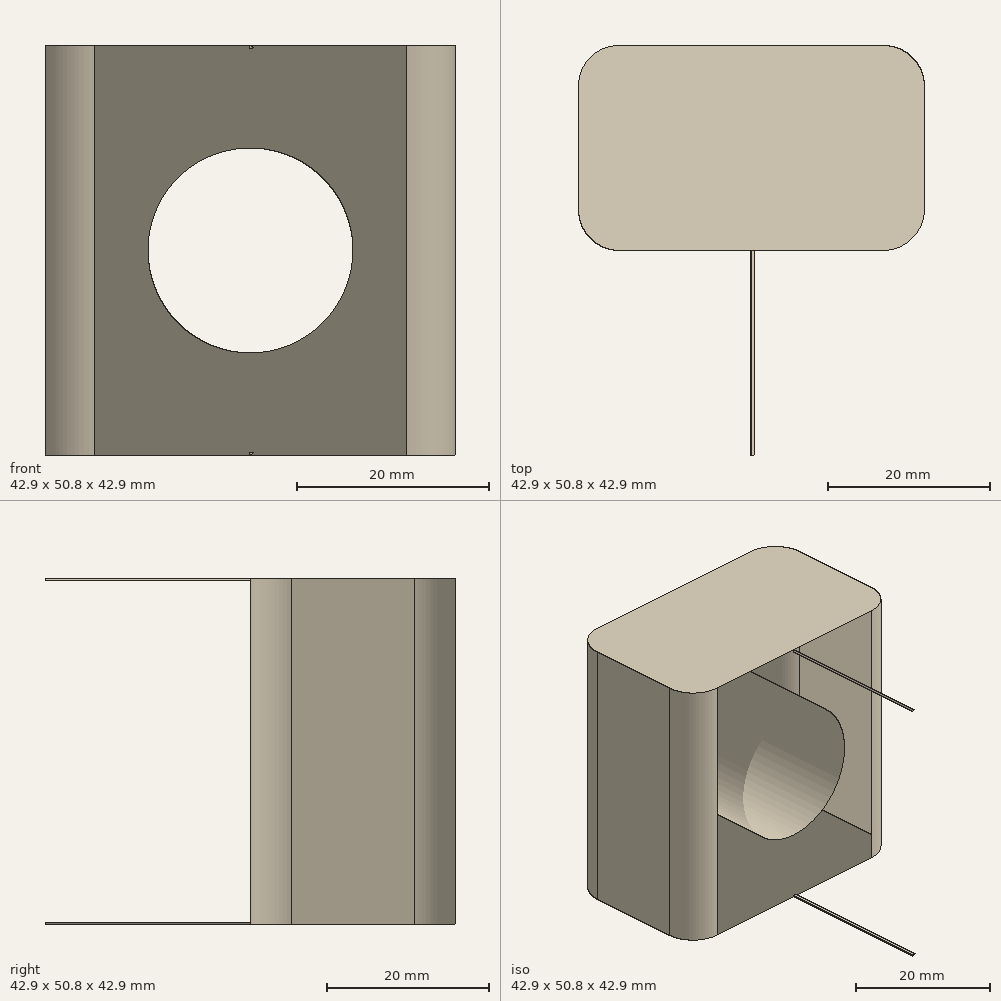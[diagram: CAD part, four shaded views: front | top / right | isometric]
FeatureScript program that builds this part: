
annotation { "Feature Type Name" : "Feature", "Feature Type Description" : "" }
export const myFeature = defineFeature(function(context is Context, id is Id, definition is map)
    precondition{}
    {
        {
            var Q0;
            Q0=qCreatedBy(makeId("Front.planeOp"),FACE);
            var sketch = newSketch(context, id + "F0", { "sketchPlane" : qUnion([Q0])});
            skLineSegment(sketch, "E0.bottom", {"start": v(-21.44, 21.44) * mm, "end": v(21.44, 21.44) * mm});
            skLineSegment(sketch, "E0.top", {"start": v(-21.44, -21.44) * mm, "end": v(21.44, -21.44) * mm});
            skLineSegment(sketch, "E0.left", {"start": v(-21.44, 21.44) * mm, "end": v(-21.44, -21.44) * mm});
            skLineSegment(sketch, "E0.right", {"start": v(21.44, 21.44) * mm, "end": v(21.44, -21.44) * mm});
            skPoint(sketch, "E0.middle", {"position": v(0, 0) * mm});
            skCircle(sketch, "E1", {"center": v(0, 0) * mm, "radius": 10.72 * mm});
            skSolve(sketch);
        }
        {
            var Q0;
            Q0=makeQuery(id+"F0.imprint","IMPRINT",FACE,{"disambiguationData":[TD([[makeQuery(id+"F0.imprint","IMPRINT",EDGE,{"derivedFrom":sQuery(id+"F0.wireOp",EDGE,"E0.bottom")}),-1.0]])]});
            extrude(context, id + "F1", {"entities" : qUnion([Q0]), "depth" : 25.4 * mm, "offsetDistance" : 25.4 * mm});
        }
        {
            var Q0;
            Q0=makeQuery(id+"F1.opExtrude","CAP_FACE",FACE,{"disambiguationData":[OSD([sQuery(id+"F0.wireOp",EDGE,"E0.bottom"),sQuery(id+"F0.wireOp",EDGE,"E0.top"),sQuery(id+"F0.wireOp",EDGE,"E0.left"),sQuery(id+"F0.wireOp",EDGE,"E0.right"),sQuery(id+"F0.wireOp",EDGE,"E1")])],"isStart":false});
            var sketch = newSketch(context, id + "F2", { "sketchPlane" : qUnion([Q0])});
            skFitSpline(sketch, "E2.MirrorC", {"points": [v(0, -21.44) * mm, v(-31.8, -40.34) * mm, v(-17.9, -101.47) * mm, v(-24.58, -66.76) * mm, v(-14.18, -69.87) * mm, v(-23.15, -57.45) * mm, v(21.44, -85.42) * mm, v(-17.46, -47.72) * mm, v(9.77, -59.73) * mm, v(-11.7, -36.11) * mm, v(0, -21.44) * mm]});
            skFitSpline(sketch, "E3.MirrorC", {"points": [v(0, -21.44) * mm, v(10.1, -51.1) * mm, v(56.97, -85.03) * mm, v(23.52, -53.99) * mm, v(53.05, -53.56) * mm, v(16.41, -38.66) * mm, v(46.61, -40.4) * mm, v(14.47, -25.9) * mm, v(0, -21.44) * mm]});
            skLineSegment(sketch, "E4.0", {"start": v(-21.44, -21.44) * mm, "end": v(-6.5, -21.44) * mm});
            skLineSegment(sketch, "E5.trimOffspring", {"start": v(4.65, -21.44) * mm, "end": v(21.44, -21.44) * mm});
            skLineSegment(sketch, "E6", {"start": v(-0.18, -21.15) * mm, "end": v(0.33, -21.15) * mm});
            skSolve(sketch);
        }
        {
            var Q0;
            Q0=makeQuery(id+"F1.opExtrude","CAP_EDGE",EDGE,{"disambiguationData":[OSD([sQuery(id+"F0.wireOp",EDGE,"E0.right")])],"isStart":true});
            var Q1;
            Q1=makeQuery(id+"F1.opExtrude","CAP_EDGE",EDGE,{"disambiguationData":[OSD([sQuery(id+"F0.wireOp",EDGE,"E0.right")])],"isStart":false});
            var Q2;
            Q2=makeQuery(id+"F1.opExtrude","CAP_EDGE",EDGE,{"disambiguationData":[OSD([sQuery(id+"F0.wireOp",EDGE,"E0.left")])],"isStart":true});
            var Q3;
            Q3=makeQuery(id+"F1.opExtrude","CAP_EDGE",EDGE,{"disambiguationData":[OSD([sQuery(id+"F0.wireOp",EDGE,"E0.left")])],"isStart":false});
            fillet(context, id + "F3", {"entities" : qUnion([Q0, Q1, Q2, Q3]), "radius" : 5.08 * mm, "tangentPropagation" : true, "allowEdgeOverflow" : false});
        }
        {
            var Q0;
            {var subQ4=sQuery(id+"F2.wireOp",EDGE,"E2.MirrorC");var subQ6=makeQuery(id+"F2.imprint","IMPRINT",VERTEX,{"derivedFrom":subQ4});Q0=makeQuery(id+"F2.imprint","IMPRINT",FACE,{"disambiguationData":[TD([[makeQuery(id+"F2.imprint","IMPRINT",EDGE,{"disambiguationData":[TD([[subQ6,-1.0]])],"derivedFrom":subQ4}),1.0]])]});}
            var Q1;
            {var subQ0=sQuery(id+"F2.wireOp",EDGE,"E6");Q1=makeQuery(id+"F2.imprint","IMPRINT",FACE,{"disambiguationData":[TD([[makeQuery(id+"F2.imprint","IMPRINT",EDGE,{"derivedFrom":subQ0}),-1.0]])]});}
            extrude(context, id + "F4", {"entities" : qUnion([Q0, Q1]), "operationType" : NewBodyOperationType.ADD, "depth" : 25.4 * mm, "offsetDistance" : 25.4 * mm});
        }
        {
            var Q0;
            Q0=makeQuery(id+"F1.opExtrude","SWEPT_BODY",BODY,{"disambiguationData":[OSD([sQuery(id+"F0.wireOp",EDGE,"E0.bottom"),sQuery(id+"F0.wireOp",EDGE,"E0.top"),sQuery(id+"F0.wireOp",EDGE,"E0.left"),sQuery(id+"F0.wireOp",EDGE,"E0.right"),sQuery(id+"F0.wireOp",EDGE,"E1")])]});
            var Q1;
            Q1=qCreatedBy(makeId("Top.planeOp"),FACE);
            mirror(context, id + "F5", {"operationType" : NewBodyOperationType.ADD, "entities" : qUnion([Q0]), "mirrorPlane" : qUnion([Q1])});
        }
        {
            var Q0;
            Q0=makeQuery(id+"F1.opExtrude","SWEPT_FACE",FACE,{"disambiguationData":[OSD([sQuery(id+"F0.wireOp",EDGE,"E0.right")])]});
            var sketch = newSketch(context, id + "F6", { "sketchPlane" : qUnion([Q0])});
            skPoint(sketch, "E7.0", {"position": v(-25.4, -101.47) * mm});
            skPoint(sketch, "E8.0", {"position": v(-25.4, -21.44) * mm});
            skPoint(sketch, "E9.0", {"position": v(-25.4, 21.44) * mm});
            skFitSpline(sketch, "E10.0", {"points": [v(-25.4, 21.44) * mm, v(-25.4, 48.18) * mm, v(-25.4, 74.93) * mm, v(-25.4, 101.67) * mm]});
            skArc(sketch, "E11", {"start": v(-25.4, -21.44) * mm, "mid": v(-35.19, -61.45) * mm, "end": v(-25.4, -101.47) * mm});
            skArc(sketch, "E12.MirrorCS", {"start": v(-25.4, 21.44) * mm, "mid": v(-35.19, 61.45) * mm, "end": v(-25.4, 101.47) * mm});
            skLineSegment(sketch, "E13.0", {"start": v(-25.4, -20.82) * mm, "end": v(-25.4, -101.67) * mm});
            skFitSpline(sketch, "E14.0", {"points": [v(-50.8, -22.4) * mm, v(-50.8, -43.44) * mm, v(-50.8, -64.49) * mm, v(-50.8, -85.53) * mm]});
            skFitSpline(sketch, "E15.0", {"points": [v(-50.8, 22.4) * mm, v(-50.8, 43.44) * mm, v(-50.8, 64.49) * mm, v(-50.8, 85.53) * mm]});
            skArc(sketch, "E16", {"start": v(-50.8, -85.53) * mm, "mid": v(-40.67, -97.6) * mm, "end": v(-25.4, -101.47) * mm});
            skArc(sketch, "E17", {"start": v(-50.8, -85.53) * mm, "mid": v(-44.2, -53.96) * mm, "end": v(-50.8, -22.4) * mm});
            skArc(sketch, "E18", {"start": v(-50.8, -22.4) * mm, "mid": v(-37.88, -25.21) * mm, "end": v(-25.4, -20.82) * mm});
            skArc(sketch, "E19.MirrorCS", {"start": v(-50.8, 85.53) * mm, "mid": v(-44.2, 53.96) * mm, "end": v(-50.8, 22.4) * mm});
            skArc(sketch, "E20.MirrorCS", {"start": v(-50.8, 85.53) * mm, "mid": v(-40.67, 97.6) * mm, "end": v(-25.4, 101.47) * mm});
            skArc(sketch, "E21.MirrorCS", {"start": v(-50.8, 22.4) * mm, "mid": v(-37.88, 25.21) * mm, "end": v(-25.4, 20.82) * mm});
            skSolve(sketch);
        }
        {
            var Q0;
            {var subQ0=sQuery(id+"F6.wireOp",EDGE,"E12.MirrorCS");Q0=makeQuery(id+"F6.imprint","IMPRINT",FACE,{"disambiguationData":[TD([[makeQuery(id+"F6.imprint","IMPRINT",EDGE,{"derivedFrom":subQ0}),-1.0]])]});}
            var Q1;
            Q1=makeQuery(id+"F6.imprint","IMPRINT",FACE,{"disambiguationData":[TD([[makeQuery(id+"F6.imprint","IMPRINT",EDGE,{"derivedFrom":sQuery(id+"F6.wireOp",EDGE,"E15.0")}),-1.0]])]});
            var Q2;
            {var subQ0=sQuery(id+"F6.wireOp",EDGE,"E11");Q2=makeQuery(id+"F6.imprint","IMPRINT",FACE,{"disambiguationData":[TD([[makeQuery(id+"F6.imprint","IMPRINT",EDGE,{"derivedFrom":subQ0}),1.0]])]});}
            var Q3;
            Q3=makeQuery(id+"F6.imprint","IMPRINT",FACE,{"disambiguationData":[TD([[makeQuery(id+"F6.imprint","IMPRINT",EDGE,{"derivedFrom":sQuery(id+"F6.wireOp",EDGE,"E14.0")}),1.0]])]});
            extrude(context, id + "F7", {"entities" : qUnion([Q0, Q1, Q2, Q3]), "operationType" : NewBodyOperationType.REMOVE, "endBound" : BoundingType.SYMMETRIC, "depth" : 182.37 * mm, "offsetDistance" : 25.4 * mm});
        }
        {
            var Q0;
            Q0=makeQuery(id+"F1.opExtrude","SWEPT_FACE",FACE,{"disambiguationData":[OSD([sQuery(id+"F0.wireOp",EDGE,"E0.left")])]});
            var sketch = newSketch(context, id + "F8", { "sketchPlane" : qUnion([Q0])});
            skLineSegment(sketch, "E22.0.0", {"start": v(50.8, 57.45) * mm, "end": v(35.1, 57.45) * mm});
            skArc(sketch, "E22.0.1", {"start": v(35.1, 57.45) * mm, "mid": v(33.16, 80.1) * mm, "end": v(25.4, 101.47) * mm});
            skFitSpline(sketch, "E22.0.2", {"points": [v(25.4, 101.47) * mm, v(25.4, 101.54) * mm, v(25.4, 101.6) * mm, v(25.4, 101.67) * mm]});
            skArc(sketch, "E22.0.3", {"start": v(25.4, 21.44) * mm, "mid": v(35.19, 61.45) * mm, "end": v(25.4, 101.47) * mm});
            skFitSpline(sketch, "E22.0.4", {"points": [v(25.4, 21.44) * mm, v(25.4, 21.23) * mm, v(25.4, 21.03) * mm, v(25.4, 20.82) * mm]});
            skLineSegment(sketch, "E22.0.5", {"start": v(25.4, 21.15) * mm, "end": v(50.8, 21.15) * mm});
            skArc(sketch, "E23.0.0", {"start": v(25.4, -101.47) * mm, "mid": v(33.16, -80.1) * mm, "end": v(35.1, -57.45) * mm});
            skLineSegment(sketch, "E23.0.1", {"start": v(35.1, -57.45) * mm, "end": v(50.8, -57.45) * mm});
            skLineSegment(sketch, "E23.0.3", {"start": v(50.8, -21.15) * mm, "end": v(25.4, -21.15) * mm});
            skArc(sketch, "E23.0.5", {"start": v(25.4, -101.47) * mm, "mid": v(35.19, -61.45) * mm, "end": v(25.4, -21.44) * mm});
            skFitSpline(sketch, "E23.0.6", {"points": [v(25.4, -101.47) * mm, v(25.4, -101.54) * mm, v(25.4, -101.6) * mm, v(25.4, -101.67) * mm]});
            skPoint(sketch, "E24.0", {"position": v(50.8, -21.16) * mm});
            skPoint(sketch, "E25.0", {"position": v(50.8, 21.16) * mm});
            skArc(sketch, "E26", {"start": v(50.8, 21.16) * mm, "mid": v(78.36, 74.11) * mm, "end": v(25.4, 101.67) * mm});
            skArc(sketch, "E27.MirrorCS", {"start": v(50.8, -21.16) * mm, "mid": v(78.36, -74.11) * mm, "end": v(25.4, -101.67) * mm});
            skSolve(sketch);
        }
    });
